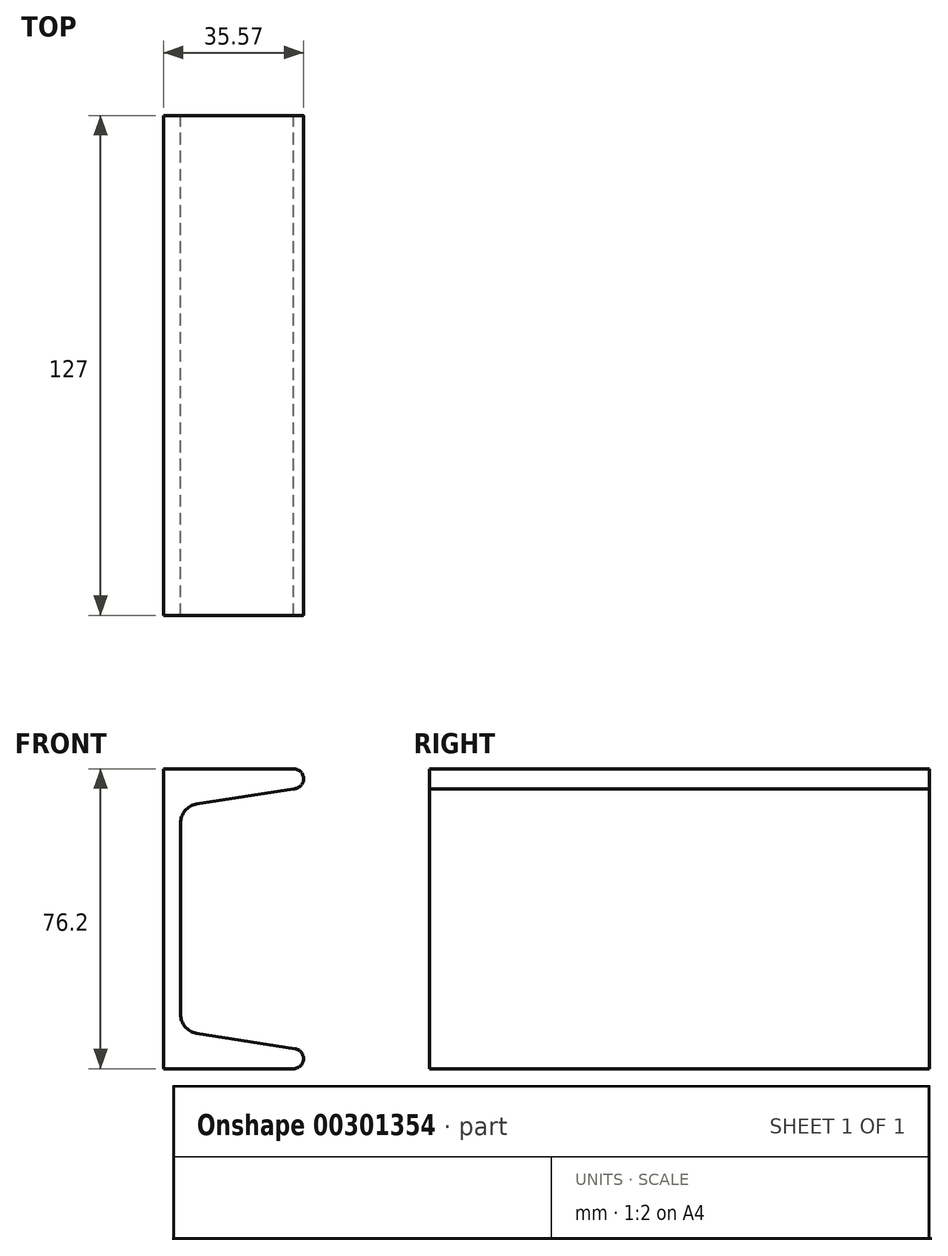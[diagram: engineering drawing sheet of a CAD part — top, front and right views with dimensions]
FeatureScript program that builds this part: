
annotation { "Feature Type Name" : "Feature", "Feature Type Description" : "" }
export const myFeature = defineFeature(function(context is Context, id is Id, definition is map)
    precondition{}
    {
        {
            var Q0;
            Q0=qCreatedBy(makeId("Front.planeOp"),FACE);
            var sketch = newSketch(context, id + "F0", { "sketchPlane" : qUnion([Q0])});
            skLineSegment(sketch, "E0", {"start": v(0, 76.2) * mm, "end": v(0, 0) * mm});
            skLineSegment(sketch, "E1", {"start": v(0, 0) * mm, "end": v(33.02, 0) * mm});
            skLineSegment(sketch, "E2", {"start": v(0, 76.2) * mm, "end": v(33.02, 76.2) * mm});
            skLineSegment(sketch, "E3", {"start": v(4.32, 62.43) * mm, "end": v(4.32, 13.8) * mm});
            skLineSegment(sketch, "E4", {"start": v(8.41, 9.01) * mm, "end": v(33.42, 5.05) * mm});
            skLineSegment(sketch, "E5", {"start": v(8.41, 67.22) * mm, "end": v(33.02, 71.12) * mm});
            skArc(sketch, "E6", {"start": v(33.02, 71.12) * mm, "mid": v(35.56, 73.66) * mm, "end": v(33.02, 76.2) * mm});
            skArc(sketch, "E7", {"start": v(33.02, 0) * mm, "mid": v(35.56, 2.34) * mm, "end": v(33.42, 5.05) * mm});
            skPoint(sketch, "E8.visualSharp", {"position": v(4.32, 9.66) * mm});
            skArc(sketch, "E8.filletArc", {"start": v(4.32, 13.8) * mm, "mid": v(5.48, 10.65) * mm, "end": v(8.41, 9.01) * mm});
            skPoint(sketch, "E9.visualSharp", {"position": v(4.32, 66.57) * mm});
            skArc(sketch, "E9.filletArc", {"start": v(8.41, 67.22) * mm, "mid": v(5.48, 65.58) * mm, "end": v(4.32, 62.43) * mm});
            skSolve(sketch);
        }
        {
            var Q0;
            Q0 = qSketchRegion(id + "F0", true);
            extrude(context, id + "F1", {"entities" : qUnion([Q0]), "depth" : 127 * mm});
        }
    });
